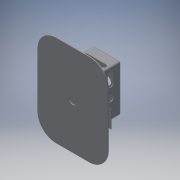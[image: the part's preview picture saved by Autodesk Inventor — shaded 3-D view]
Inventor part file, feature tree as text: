
AUTODESK INVENTOR PART (.ipt)
format: ipt  version: 2018 (Build 220112000, 112)  size: 373,760 bytes
history: native  units: in
note: dims shown in document units (in); Inventor stores cm internally (conversion verified against a paired STEP export)
features: extrude x7, sketch x7, other x3, fillet x2, shell x1, reference x1
ambient origin geometry x8: Origin, YZ Plane, XZ Plane, XY Plane, X Axis, Y Axis, Z Axis, Center Point
bodies: Solid1 (feature_tree)
feature tree (21):
  extrude  "Extrusion1"  Depth=590.5512in
  shell  "Shell2"  Thickness=11.811in
  extrude  "Extrusion2"  Depth=118.1102in
  extrude  "Extrusion4"  Depth=39.3701in
  fillet  "Fillet1"  Radius=568.3312in
  extrude  "Extrusion5"  Depth=393.7008in
  extrude  "Extrusion6"  Depth=202.7475in TaperAngle=0.0deg
  extrude  "Extrusion7"  [1 undecoded]
  extrude  "Extrusion8"  [1 undecoded]
  fillet  "Fillet2"  [1 undecoded]
  sketch  "Sketch1"  dims[d0=984.252in d1=590.5512in]
  sketch  "Sketch3"  dims[d2=309.5812in d3=405.97in d4=0.0137in d5=0.0in d7=11.811in]
  reference  "Reference1"
  sketch  "Sketch4"  dims[d8=568.3312in d9=0.0in d10=118.1102in]
  sketch  "Sketch5"  dims[d13=568.3312in d14=0.0in d15=39.3701in d16=568.3312in d17=0.0in]
  sketch  "Sketch6"  dims[d18=196.8504in d19=0.0in d21=393.7008in]
  sketch  "Sketch8"  dims[d22=19.685in d23=0.0in d24=202.7475in d25=0.0in]
  sketch  "Sketch9"  dims[d26=7.874in]
  parser-record x1  (decoder bookkeeping rows leaked as tree rows — omitted from the tree; the rows remain in map.json)
  other  "Assembly1.iam"
  other  "transmission box:1"
note: 3 required parameter values undecoded (feature->parameter linkage not recoverable at this tier; creation-order binding heuristic only, values carry confidence <= 0.55)
note: 1 file-system path scrubbed to <path> (originals preserved in map.json)
